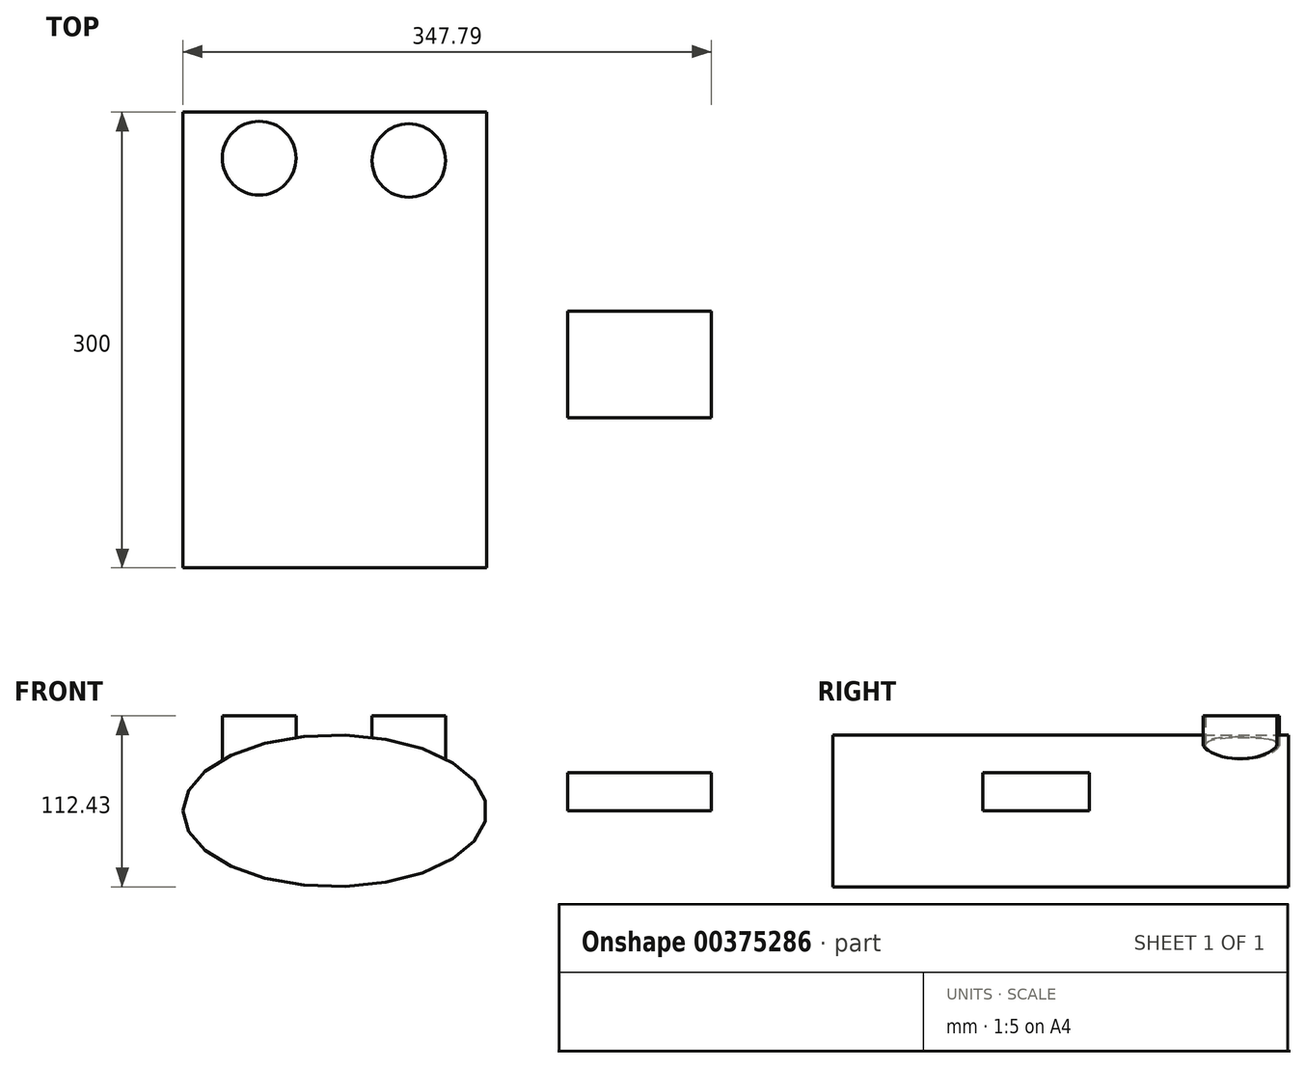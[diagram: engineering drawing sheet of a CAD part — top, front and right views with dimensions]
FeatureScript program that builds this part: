
annotation { "Feature Type Name" : "Feature", "Feature Type Description" : "" }
export const myFeature = defineFeature(function(context is Context, id is Id, definition is map)
    precondition{}
    {
        {
            var Q0;
            Q0=qCreatedBy(makeId("Front.planeOp"),FACE);
            var sketch = newSketch(context, id + "F0", { "sketchPlane" : qUnion([Q0])});
            skEllipse(sketch, "E0", {"center": v(0, 0) * mm, "majorRadius": 100 * mm, "minorRadius": 50 * mm, "majorAxis": v(-1, 0)});
            skSolve(sketch);
        }
        {
            var Q0;
            Q0=makeQuery(id+"F0.imprint","IMPRINT",FACE,{"disambiguationData":[TD([[makeQuery(id+"F0.imprint","IMPRINT",EDGE,{"derivedFrom":sQuery(id+"F0.wireOp",EDGE,"E0")}),1.0]])]});
            extrude(context, id + "F1", {"entities" : qUnion([Q0]), "depth" : 300 * mm});
        }
        {
            var Q0;
            Q0=qCreatedBy(makeId("Top.planeOp"),FACE);
            var sketch = newSketch(context, id + "F2", { "sketchPlane" : qUnion([Q0])});
            skCircle(sketch, "E1", {"center": v(-49.89, -30.22) * mm, "radius": 24.27 * mm});
            skCircle(sketch, "E2", {"center": v(48.66, -31.8) * mm, "radius": 24.21 * mm});
            skSolve(sketch);
        }
        {
            var Q0;
            Q0 = qSketchRegion(id + "F2", true);
            extrude(context, id + "F3", {"entities" : qUnion([Q0]), "operationType" : NewBodyOperationType.ADD, "depth" : 62.43 * mm});
        }
        {
            var Q0;
            Q0=qCreatedBy(makeId("Top.planeOp"),FACE);
            var sketch = newSketch(context, id + "F4", { "sketchPlane" : qUnion([Q0])});
            skLineSegment(sketch, "E3.bottom", {"start": v(153.14, -131.1) * mm, "end": v(247.79, -131.1) * mm});
            skLineSegment(sketch, "E3.top", {"start": v(153.14, -201.04) * mm, "end": v(247.79, -201.04) * mm});
            skLineSegment(sketch, "E3.left", {"start": v(153.14, -131.1) * mm, "end": v(153.14, -201.04) * mm});
            skLineSegment(sketch, "E3.right", {"start": v(247.79, -131.1) * mm, "end": v(247.79, -201.04) * mm});
            skSolve(sketch);
        }
        {
            var Q0;
            Q0 = qSketchRegion(id + "F4", true);
            extrude(context, id + "F5", {"entities" : qUnion([Q0]), "depth" : 25 * mm});
        }
    });
